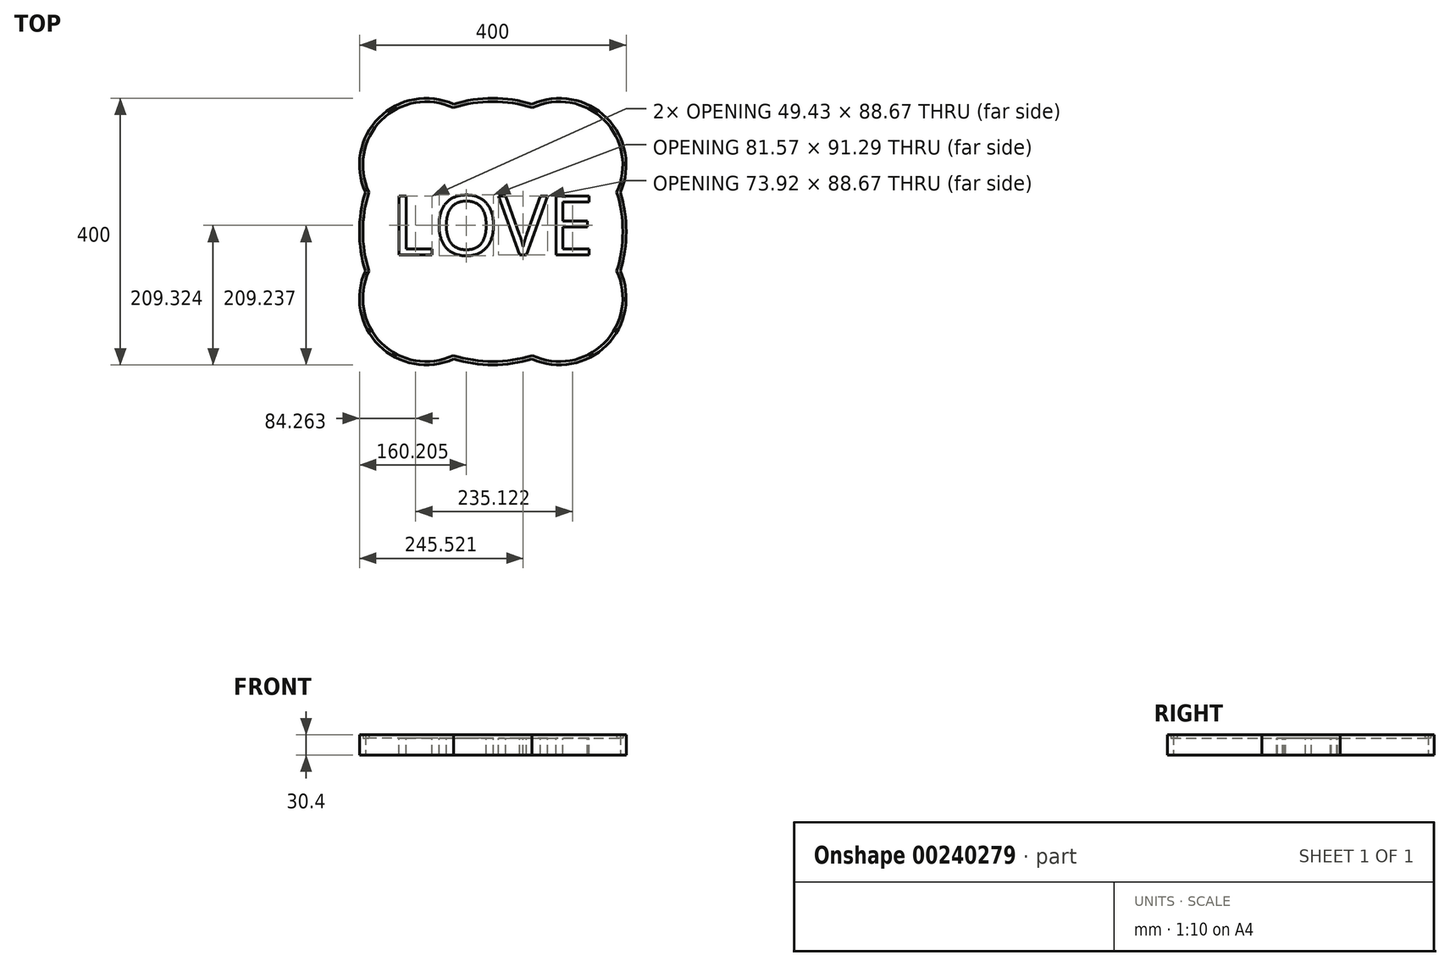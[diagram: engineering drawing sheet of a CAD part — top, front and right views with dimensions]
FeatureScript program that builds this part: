
annotation { "Feature Type Name" : "Feature", "Feature Type Description" : "" }
export const myFeature = defineFeature(function(context is Context, id is Id, definition is map)
    precondition{}
    {
        {
            var Q0;
            Q0=qCreatedBy(makeId("Top.planeOp"),FACE);
            var sketch = newSketch(context, id + "F0", { "sketchPlane" : qUnion([Q0])});
            skArc(sketch, "E0", {"start": v(-191.14, 58.86) * mm, "mid": v(-200, 0) * mm, "end": v(-191.14, -58.86) * mm});
            skLineSegment(sketch, "E1.bottom", {"start": v(-100, 100) * mm, "end": v(100, 100) * mm, "construction": true});
            skLineSegment(sketch, "E1.top", {"start": v(-100, -100) * mm, "end": v(100, -100) * mm, "construction": true});
            skLineSegment(sketch, "E1.left", {"start": v(-100, 100) * mm, "end": v(-100, -100) * mm, "construction": true});
            skLineSegment(sketch, "E1.right", {"start": v(100, 100) * mm, "end": v(100, -100) * mm, "construction": true});
            skArc(sketch, "E2", {"start": v(-58.86, 191.14) * mm, "mid": v(-170.71, 170.71) * mm, "end": v(-191.14, 58.86) * mm});
            skArc(sketch, "E3", {"start": v(191.14, 58.86) * mm, "mid": v(170.71, 170.71) * mm, "end": v(58.86, 191.14) * mm});
            skArc(sketch, "E4", {"start": v(-191.14, -58.86) * mm, "mid": v(-170.71, -170.71) * mm, "end": v(-58.86, -191.14) * mm});
            skArc(sketch, "E5", {"start": v(58.86, -191.14) * mm, "mid": v(170.71, -170.71) * mm, "end": v(191.14, -58.86) * mm});
            skArc(sketch, "E6.trimOffspring", {"start": v(58.86, 191.14) * mm, "mid": v(0, 200) * mm, "end": v(-58.86, 191.14) * mm});
            skArc(sketch, "E7.trimOffspring", {"start": v(191.14, -58.86) * mm, "mid": v(200, 0) * mm, "end": v(191.14, 58.86) * mm});
            skArc(sketch, "E8.trimOffspring", {"start": v(-58.86, -191.14) * mm, "mid": v(0, -200) * mm, "end": v(58.86, -191.14) * mm});
            skSolve(sketch);
        }
        {
            var Q0;
            Q0=makeQuery(id+"F0.imprint","IMPRINT",FACE,{"disambiguationData":[TD([[makeQuery(id+"F0.imprint","IMPRINT",EDGE,{"derivedFrom":sQuery(id+"F0.wireOp",EDGE,"E0")}),1.0]])]});
            extrude(context, id + "F1", {"entities" : qUnion([Q0]), "depth" : 25.4 * mm});
        }
        {
            var Q0;
            Q0=makeQuery(id+"F1.opExtrude","CAP_FACE",FACE,{"disambiguationData":[OSD([sQuery(id+"F0.wireOp",EDGE,"E0"),sQuery(id+"F0.wireOp",EDGE,"E2"),sQuery(id+"F0.wireOp",EDGE,"E3"),sQuery(id+"F0.wireOp",EDGE,"E4"),sQuery(id+"F0.wireOp",EDGE,"E5"),sQuery(id+"F0.wireOp",EDGE,"E6.trimOffspring"),sQuery(id+"F0.wireOp",EDGE,"E7.trimOffspring"),sQuery(id+"F0.wireOp",EDGE,"E8.trimOffspring")])],"isStart":false});
            var sketch = newSketch(context, id + "F2", { "sketchPlane" : qUnion([Q0])});
            skText(sketch, "E9", { "text": "LOVE", "fontName": "OpenSans-Regular.ttf"});
            const initialGuessF2  = {"E9": [-0.15264, -0.0351, 1, 0, 0.08943]};
            skSetInitialGuess(sketch, initialGuessF2);
            skSolve(sketch);
        }
        {
            var Q0;
            Q0 = qSketchRegion(id + "F2", true);
            extrude(context, id + "F3", {"entities" : qUnion([Q0]), "operationType" : NewBodyOperationType.REMOVE, "oppositeDirection" : true, "depth" : 25.4 * mm});
        }
        {
            var Q0;
            {var subQ0=sQuery(id+"F0.wireOp",EDGE,"E3");var subQ1=sQuery(id+"F0.wireOp",EDGE,"E6.trimOffspring");var subQ2=sQuery(id+"F0.wireOp",EDGE,"E0");var subQ3=sQuery(id+"F0.wireOp",EDGE,"E4");var subQ4=sQuery(id+"F0.wireOp",EDGE,"E2");var subQ5=sQuery(id+"F0.wireOp",EDGE,"E5");var subQ6=sQuery(id+"F0.wireOp",EDGE,"E7.trimOffspring");var subQ7=sQuery(id+"F0.wireOp",EDGE,"E8.trimOffspring");Q0=makeQuery(id+"F3.boolean.opBoolean","SPLIT",FACE,{"disambiguationData":[TD([makeQuery(id+"F1.opExtrude","SWEPT_FACE",FACE,{"disambiguationData":[OSD([subQ2])]})])],"derivedFrom":makeQuery(id+"F1.opExtrude","CAP_FACE",FACE,{"disambiguationData":[OSD([subQ2,subQ4,subQ0,subQ3,subQ5,subQ1,subQ6,subQ7])],"isStart":false})});}
            var sketch = newSketch(context, id + "F4", { "sketchPlane" : qUnion([Q0])});
            skArc(sketch, "E10.0", {"start": v(-59.2, -185.8) * mm, "mid": v(0, -195) * mm, "end": v(59.2, -185.8) * mm});
            skArc(sketch, "E10.1", {"start": v(-185.8, -59.2) * mm, "mid": v(-167.18, -167.18) * mm, "end": v(-59.2, -185.8) * mm});
            skArc(sketch, "E10.2", {"start": v(59.2, -185.8) * mm, "mid": v(167.18, -167.18) * mm, "end": v(185.8, -59.2) * mm});
            skArc(sketch, "E10.3", {"start": v(-185.8, 59.2) * mm, "mid": v(-195, 0) * mm, "end": v(-185.8, -59.2) * mm});
            skArc(sketch, "E10.4", {"start": v(185.8, -59.2) * mm, "mid": v(195, 0) * mm, "end": v(185.8, 59.2) * mm});
            skArc(sketch, "E10.5", {"start": v(185.8, 59.2) * mm, "mid": v(167.18, 167.18) * mm, "end": v(59.2, 185.8) * mm});
            skArc(sketch, "E10.6", {"start": v(59.2, 185.8) * mm, "mid": v(0, 195) * mm, "end": v(-59.2, 185.8) * mm});
            skArc(sketch, "E10.7", {"start": v(-59.2, 185.8) * mm, "mid": v(-167.18, 167.18) * mm, "end": v(-185.8, 59.2) * mm});
            skPoint(sketch, "E11.0", {"position": v(-170.71, 170.71) * mm});
            skArc(sketch, "E12.0", {"start": v(-58.86, 191.14) * mm, "mid": v(-170.71, 170.71) * mm, "end": v(-191.14, 58.86) * mm});
            skArc(sketch, "E13.0", {"start": v(58.86, 191.14) * mm, "mid": v(0, 200) * mm, "end": v(-58.86, 191.14) * mm});
            skArc(sketch, "E14.0", {"start": v(191.14, 58.86) * mm, "mid": v(170.71, 170.71) * mm, "end": v(58.86, 191.14) * mm});
            skArc(sketch, "E15.0", {"start": v(191.14, -58.86) * mm, "mid": v(200, 0) * mm, "end": v(191.14, 58.86) * mm});
            skArc(sketch, "E16.0", {"start": v(58.86, -191.14) * mm, "mid": v(170.71, -170.71) * mm, "end": v(191.14, -58.86) * mm});
            skArc(sketch, "E17.0", {"start": v(-58.86, -191.14) * mm, "mid": v(0, -200) * mm, "end": v(58.86, -191.14) * mm});
            skArc(sketch, "E18.0", {"start": v(-191.14, -58.86) * mm, "mid": v(-170.71, -170.71) * mm, "end": v(-58.86, -191.14) * mm});
            skArc(sketch, "E19.0", {"start": v(-191.14, 58.86) * mm, "mid": v(-200, 0) * mm, "end": v(-191.14, -58.86) * mm});
            skSolve(sketch);
        }
        {
            var Q0;
            Q0=makeQuery(id+"F4.imprint","IMPRINT",FACE,{"disambiguationData":[TD([[makeQuery(id+"F4.imprint","IMPRINT",EDGE,{"derivedFrom":sQuery(id+"F4.wireOp",EDGE,"E10.0")}),-1.0]])]});
            extrude(context, id + "F5", {"entities" : qUnion([Q0]), "operationType" : NewBodyOperationType.ADD, "depth" : 5 * mm});
        }
    });
